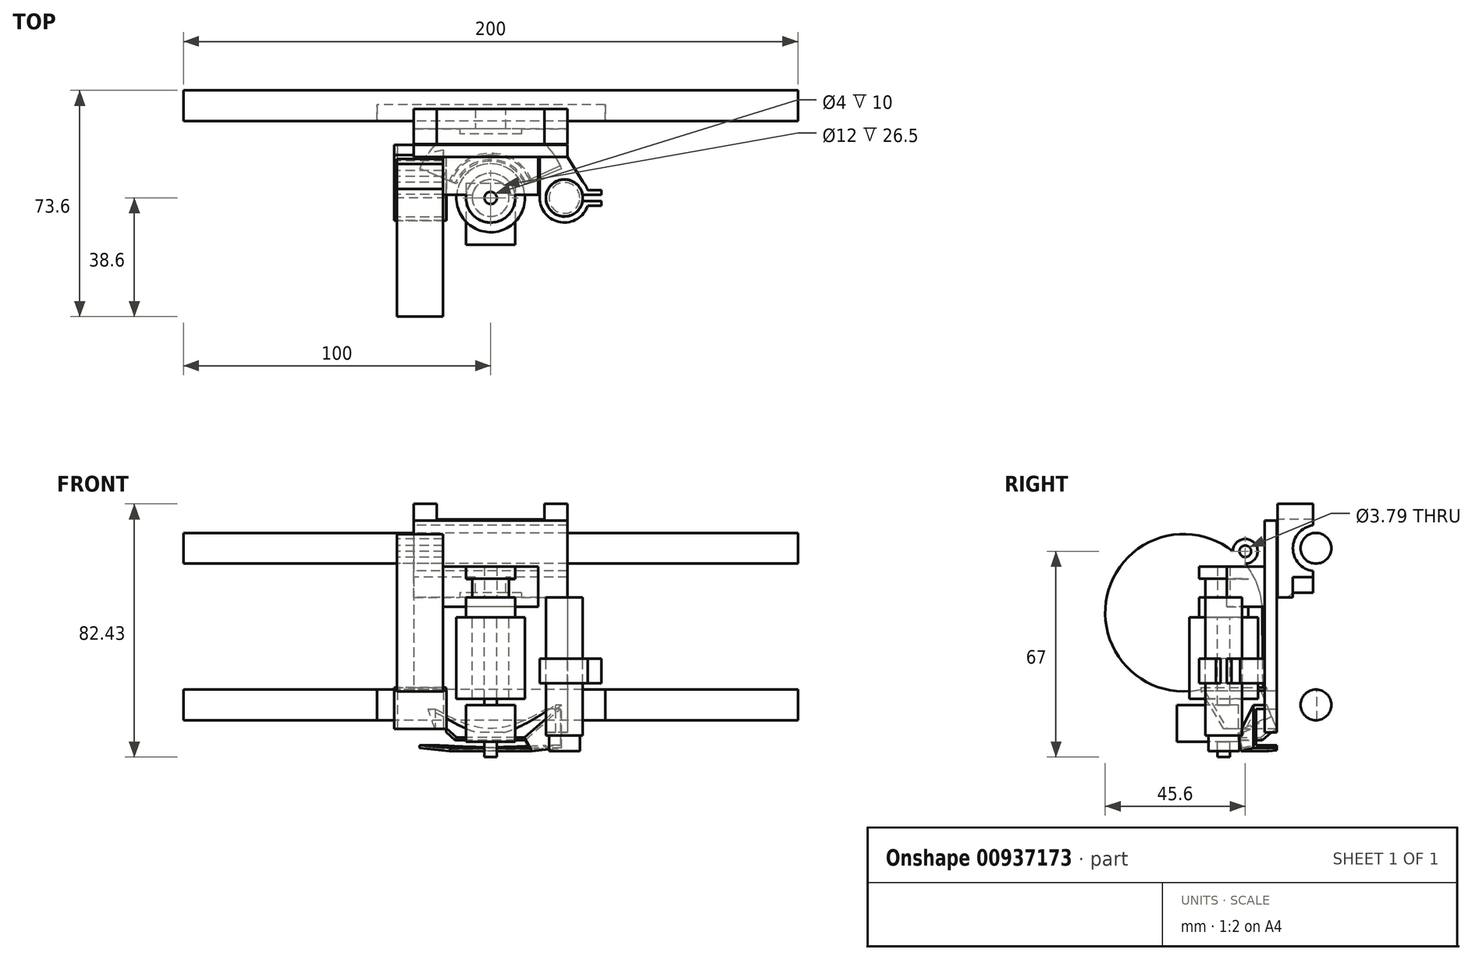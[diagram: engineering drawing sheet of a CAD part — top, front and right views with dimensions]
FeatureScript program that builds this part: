
annotation { "Feature Type Name" : "Feature", "Feature Type Description" : "" }
export const myFeature = defineFeature(function(context is Context, id is Id, definition is map)
    precondition{}
    {
        {
            var Q0;
            Q0=qCreatedBy(makeId("Top.planeOp"),FACE);
            var sketch = newSketch(context, id + "F0", { "sketchPlane" : qUnion([Q0])});
            skCircle(sketch, "E0", {"center": v(0, 0) * mm, "radius": 8 * mm});
            skCircle(sketch, "E1", {"center": v(0, 0) * mm, "radius": 6 * mm});
            skCircle(sketch, "E2", {"center": v(0, 0) * mm, "radius": 11.15 * mm});
            skCircle(sketch, "E3", {"center": v(0, 0) * mm, "radius": 2 * mm});
            skLineSegment(sketch, "E4.bottom", {"start": v(-8, 4.8) * mm, "end": v(8, 4.8) * mm});
            skLineSegment(sketch, "E4.top", {"start": v(-8, -15.2) * mm, "end": v(8, -15.2) * mm});
            skLineSegment(sketch, "E4.left", {"start": v(-8, 4.8) * mm, "end": v(-8, -15.2) * mm});
            skLineSegment(sketch, "E4.right", {"start": v(8, 4.8) * mm, "end": v(8, -15.2) * mm});
            skCircle(sketch, "E5", {"center": v(24, 0) * mm, "radius": 6 * mm});
            skCircle(sketch, "E6", {"center": v(24, 0) * mm, "radius": 5 * mm});
            skLineSegment(sketch, "E7", {"start": v(-23, 26.47) * mm, "end": v(-23, -35) * mm, "construction": true});
            skSolve(sketch);
        }
        {
            var Q0;
            Q0=makeQuery(id+"F0.imprint","IMPRINT",FACE,{"disambiguationData":[TD([[makeQuery(id+"F0.imprint","IMPRINT",EDGE,{"derivedFrom":sQuery(id+"F0.wireOp",EDGE,"E3")}),-1.0]])]});
            var Q1;
            {var subQ0=sQuery(id+"F0.wireOp",EDGE,"E4.bottom");var subQ1=sQuery(id+"F0.wireOp",EDGE,"E1");var subQ2=makeQuery(id+"F0.imprint","INTERSECT",VERTEX,{"disambiguationData":[OD(0.0)],"derivedFrom":[subQ1,subQ0]});Q1=makeQuery(id+"F0.imprint","IMPRINT",FACE,{"disambiguationData":[TD([[makeQuery(id+"F0.imprint","IMPRINT",EDGE,{"disambiguationData":[TD([[subQ2,1.0]])],"derivedFrom":subQ1}),1.0]])]});}
            extrude(context, id + "F1", {"entities" : qUnion([Q0, Q1]), "depth" : 6.05 * mm, "offsetDistance" : 25 * mm});
        }
        {
            var Q0;
            {var subQ0=sQuery(id+"F0.wireOp",EDGE,"E0");var subQ3=sQuery(id+"F0.wireOp",EDGE,"E4.bottom");var subQ8=makeQuery(id+"F0.imprint","INTERSECT",VERTEX,{"disambiguationData":[OD(0.0)],"derivedFrom":[subQ0,subQ3]});Q0=makeQuery(id+"F0.imprint","IMPRINT",FACE,{"disambiguationData":[TD([[makeQuery(id+"F0.imprint","IMPRINT",EDGE,{"disambiguationData":[TD([[subQ8,1.0]])],"derivedFrom":subQ0}),1.0]])]});}
            var Q1;
            {var subQ0=sQuery(id+"F0.wireOp",EDGE,"E4.bottom");var subQ1=sQuery(id+"F0.wireOp",EDGE,"E0");var subQ2=makeQuery(id+"F0.imprint","INTERSECT",VERTEX,{"disambiguationData":[OD(0.0)],"derivedFrom":[subQ1,subQ0]});Q1=makeQuery(id+"F0.imprint","IMPRINT",FACE,{"disambiguationData":[TD([[makeQuery(id+"F0.imprint","IMPRINT",EDGE,{"disambiguationData":[TD([[subQ2,-1.0]])],"derivedFrom":subQ1}),1.0]])]});}
            var Q2;
            Q2=makeQuery(id+"F0.imprint","IMPRINT",FACE,{"disambiguationData":[TD([[makeQuery(id+"F0.imprint","IMPRINT",EDGE,{"derivedFrom":sQuery(id+"F0.wireOp",EDGE,"E3")}),-1.0]])]});
            var Q3;
            {var subQ0=sQuery(id+"F0.wireOp",EDGE,"E4.bottom");var subQ1=sQuery(id+"F0.wireOp",EDGE,"E1");var subQ2=makeQuery(id+"F0.imprint","INTERSECT",VERTEX,{"disambiguationData":[OD(0.0)],"derivedFrom":[subQ1,subQ0]});Q3=makeQuery(id+"F0.imprint","IMPRINT",FACE,{"disambiguationData":[TD([[makeQuery(id+"F0.imprint","IMPRINT",EDGE,{"disambiguationData":[TD([[subQ2,1.0]])],"derivedFrom":subQ1}),1.0]])]});}
            extrude(context, id + "F2", {"entities" : qUnion([Q0, Q1, Q2, Q3]), "operationType" : NewBodyOperationType.ADD, "depth" : 10 * mm, "offsetDistance" : 25 * mm, "hasSecondDirection" : true, "secondDirectionOppositeDirection" : false, "secondDirectionDepth" : 6.05 * mm});
        }
        {
            var Q0;
            {var subQ0=sQuery(id+"F0.wireOp",EDGE,"E0");var subQ3=sQuery(id+"F0.wireOp",EDGE,"E4.bottom");var subQ8=makeQuery(id+"F0.imprint","INTERSECT",VERTEX,{"disambiguationData":[OD(0.0)],"derivedFrom":[subQ0,subQ3]});Q0=makeQuery(id+"F0.imprint","IMPRINT",FACE,{"disambiguationData":[TD([[makeQuery(id+"F0.imprint","IMPRINT",EDGE,{"disambiguationData":[TD([[subQ8,1.0]])],"derivedFrom":subQ0}),1.0]])]});}
            var Q1;
            {var subQ0=sQuery(id+"F0.wireOp",EDGE,"E4.bottom");var subQ1=sQuery(id+"F0.wireOp",EDGE,"E0");var subQ2=makeQuery(id+"F0.imprint","INTERSECT",VERTEX,{"disambiguationData":[OD(0.0)],"derivedFrom":[subQ1,subQ0]});Q1=makeQuery(id+"F0.imprint","IMPRINT",FACE,{"disambiguationData":[TD([[makeQuery(id+"F0.imprint","IMPRINT",EDGE,{"disambiguationData":[TD([[subQ2,-1.0]])],"derivedFrom":subQ1}),1.0]])]});}
            var Q2;
            Q2=makeQuery(id+"F0.imprint","IMPRINT",FACE,{"disambiguationData":[TD([[makeQuery(id+"F0.imprint","IMPRINT",EDGE,{"derivedFrom":sQuery(id+"F0.wireOp",EDGE,"E3")}),-1.0]])]});
            var Q3;
            {var subQ0=sQuery(id+"F0.wireOp",EDGE,"E4.bottom");var subQ1=sQuery(id+"F0.wireOp",EDGE,"E1");var subQ2=makeQuery(id+"F0.imprint","INTERSECT",VERTEX,{"disambiguationData":[OD(0.0)],"derivedFrom":[subQ1,subQ0]});Q3=makeQuery(id+"F0.imprint","IMPRINT",FACE,{"disambiguationData":[TD([[makeQuery(id+"F0.imprint","IMPRINT",EDGE,{"disambiguationData":[TD([[subQ2,1.0]])],"derivedFrom":subQ1}),1.0]])]});}
            extrude(context, id + "F3", {"entities" : qUnion([Q0, Q1, Q2, Q3]), "operationType" : NewBodyOperationType.ADD, "oppositeDirection" : true, "depth" : 6.5 * mm, "offsetDistance" : 25 * mm});
        }
        {
            var Q0;
            {var subQ0=sQuery(id+"F0.wireOp",EDGE,"E4.right");var subQ1=sQuery(id+"F0.wireOp",EDGE,"E0");var subQ2=makeQuery(id+"F0.imprint","INTERSECT",VERTEX,{"derivedFrom":[subQ1,subQ0]});Q0=makeQuery(id+"F0.imprint","IMPRINT",FACE,{"disambiguationData":[TD([[makeQuery(id+"F0.imprint","IMPRINT",EDGE,{"disambiguationData":[TD([[subQ2,1.0]])],"derivedFrom":subQ1}),-1.0]])]});}
            var Q1;
            {var subQ1=sQuery(id+"F0.wireOp",EDGE,"E4.bottom");var subQ3=sQuery(id+"F0.wireOp",EDGE,"E0");var subQ4=makeQuery(id+"F0.imprint","INTERSECT",VERTEX,{"disambiguationData":[OD(0.0)],"derivedFrom":[subQ3,subQ1]});Q1=makeQuery(id+"F0.imprint","IMPRINT",FACE,{"disambiguationData":[TD([[makeQuery(id+"F0.imprint","IMPRINT",EDGE,{"disambiguationData":[TD([[subQ4,-1.0]])],"derivedFrom":subQ3}),-1.0]])]});}
            var Q2;
            {var subQ0=sQuery(id+"F0.wireOp",EDGE,"E4.bottom");var subQ1=sQuery(id+"F0.wireOp",EDGE,"E0");var subQ2=makeQuery(id+"F0.imprint","INTERSECT",VERTEX,{"disambiguationData":[OD(0.0)],"derivedFrom":[subQ1,subQ0]});Q2=makeQuery(id+"F0.imprint","IMPRINT",FACE,{"disambiguationData":[TD([[makeQuery(id+"F0.imprint","IMPRINT",EDGE,{"disambiguationData":[TD([[subQ2,-1.0]])],"derivedFrom":subQ1}),1.0]])]});}
            var Q3;
            {var subQ0=sQuery(id+"F0.wireOp",EDGE,"E0");var subQ3=sQuery(id+"F0.wireOp",EDGE,"E4.bottom");var subQ8=makeQuery(id+"F0.imprint","INTERSECT",VERTEX,{"disambiguationData":[OD(0.0)],"derivedFrom":[subQ0,subQ3]});Q3=makeQuery(id+"F0.imprint","IMPRINT",FACE,{"disambiguationData":[TD([[makeQuery(id+"F0.imprint","IMPRINT",EDGE,{"disambiguationData":[TD([[subQ8,1.0]])],"derivedFrom":subQ0}),1.0]])]});}
            var Q4;
            {var subQ0=sQuery(id+"F0.wireOp",EDGE,"E4.bottom");var subQ1=sQuery(id+"F0.wireOp",EDGE,"E0");var subQ2=makeQuery(id+"F0.imprint","INTERSECT",VERTEX,{"disambiguationData":[OD(0.0)],"derivedFrom":[subQ1,subQ0]});Q4=makeQuery(id+"F0.imprint","IMPRINT",FACE,{"disambiguationData":[TD([[makeQuery(id+"F0.imprint","IMPRINT",EDGE,{"disambiguationData":[TD([[subQ2,1.0]])],"derivedFrom":subQ1}),-1.0]])]});}
            var Q5;
            {var subQ0=sQuery(id+"F0.wireOp",EDGE,"E4.bottom");var subQ1=sQuery(id+"F0.wireOp",EDGE,"E0");var subQ2=makeQuery(id+"F0.imprint","INTERSECT",VERTEX,{"disambiguationData":[OD(1.0)],"derivedFrom":[subQ1,subQ0]});Q5=makeQuery(id+"F0.imprint","IMPRINT",FACE,{"disambiguationData":[TD([[makeQuery(id+"F0.imprint","IMPRINT",EDGE,{"disambiguationData":[TD([[subQ2,-1.0]])],"derivedFrom":subQ1}),-1.0]])]});}
            extrude(context, id + "F4", {"entities" : qUnion([Q0, Q1, Q2, Q3, Q4, Q5]), "operationType" : NewBodyOperationType.ADD, "oppositeDirection" : true, "depth" : 33 * mm, "offsetDistance" : 25 * mm, "hasSecondDirection" : true, "secondDirectionOppositeDirection" : true, "secondDirectionDepth" : 6.5 * mm});
        }
        {
            var Q0;
            Q0=makeQuery(id+"F0.imprint","IMPRINT",FACE,{"disambiguationData":[TD([[makeQuery(id+"F0.imprint","IMPRINT",EDGE,{"derivedFrom":sQuery(id+"F0.wireOp",EDGE,"E3")}),1.0]])]});
            extrude(context, id + "F5", {"entities" : qUnion([Q0]), "operationType" : NewBodyOperationType.ADD, "oppositeDirection" : true, "depth" : 52 * mm, "offsetDistance" : 25 * mm});
        }
        {
            var Q0;
            {var subQ5=sQuery(id+"F0.wireOp",EDGE,"E4.top");Q0=makeQuery(id+"F0.imprint","IMPRINT",FACE,{"disambiguationData":[TD([[makeQuery(id+"F0.imprint","IMPRINT",EDGE,{"derivedFrom":subQ5}),1.0]])]});}
            var Q1;
            {var subQ0=sQuery(id+"F0.wireOp",EDGE,"E4.right");var subQ1=sQuery(id+"F0.wireOp",EDGE,"E0");var subQ2=makeQuery(id+"F0.imprint","INTERSECT",VERTEX,{"derivedFrom":[subQ1,subQ0]});Q1=makeQuery(id+"F0.imprint","IMPRINT",FACE,{"disambiguationData":[TD([[makeQuery(id+"F0.imprint","IMPRINT",EDGE,{"disambiguationData":[TD([[subQ2,1.0]])],"derivedFrom":subQ1}),-1.0]])]});}
            var Q2;
            {var subQ0=sQuery(id+"F0.wireOp",EDGE,"E4.bottom");var subQ1=sQuery(id+"F0.wireOp",EDGE,"E0");var subQ2=makeQuery(id+"F0.imprint","INTERSECT",VERTEX,{"disambiguationData":[OD(0.0)],"derivedFrom":[subQ1,subQ0]});Q2=makeQuery(id+"F0.imprint","IMPRINT",FACE,{"disambiguationData":[TD([[makeQuery(id+"F0.imprint","IMPRINT",EDGE,{"disambiguationData":[TD([[subQ2,1.0]])],"derivedFrom":subQ1}),-1.0]])]});}
            var Q3;
            {var subQ0=sQuery(id+"F0.wireOp",EDGE,"E0");var subQ3=sQuery(id+"F0.wireOp",EDGE,"E4.bottom");var subQ8=makeQuery(id+"F0.imprint","INTERSECT",VERTEX,{"disambiguationData":[OD(0.0)],"derivedFrom":[subQ0,subQ3]});Q3=makeQuery(id+"F0.imprint","IMPRINT",FACE,{"disambiguationData":[TD([[makeQuery(id+"F0.imprint","IMPRINT",EDGE,{"disambiguationData":[TD([[subQ8,1.0]])],"derivedFrom":subQ0}),1.0]])]});}
            var Q4;
            {var subQ0=sQuery(id+"F0.wireOp",EDGE,"E4.bottom");var subQ1=sQuery(id+"F0.wireOp",EDGE,"E0");var subQ2=makeQuery(id+"F0.imprint","INTERSECT",VERTEX,{"disambiguationData":[OD(1.0)],"derivedFrom":[subQ1,subQ0]});Q4=makeQuery(id+"F0.imprint","IMPRINT",FACE,{"disambiguationData":[TD([[makeQuery(id+"F0.imprint","IMPRINT",EDGE,{"disambiguationData":[TD([[subQ2,-1.0]])],"derivedFrom":subQ1}),-1.0]])]});}
            var Q5;
            Q5=makeQuery(id+"F0.imprint","IMPRINT",FACE,{"disambiguationData":[TD([[makeQuery(id+"F0.imprint","IMPRINT",EDGE,{"derivedFrom":sQuery(id+"F0.wireOp",EDGE,"E3")}),-1.0]])]});
            var Q6;
            Q6=makeQuery(id+"F0.imprint","IMPRINT",FACE,{"disambiguationData":[TD([[makeQuery(id+"F0.imprint","IMPRINT",EDGE,{"derivedFrom":sQuery(id+"F0.wireOp",EDGE,"E3")}),1.0]])]});
            extrude(context, id + "F6", {"entities" : qUnion([Q0, Q1, Q2, Q3, Q4, Q5, Q6]), "operationType" : NewBodyOperationType.ADD, "oppositeDirection" : true, "depth" : 47 * mm, "offsetDistance" : 25 * mm, "hasSecondDirection" : true, "secondDirectionOppositeDirection" : true, "secondDirectionDepth" : 35 * mm});
        }
        {
            var Q0;
            Q0=qCreatedBy(makeId("Right.planeOp"),FACE);
            var sketch = newSketch(context, id + "F7", { "sketchPlane" : qUnion([Q0])});
            skCircle(sketch, "E8", {"center": v(30, -35) * mm, "radius": 5 * mm});
            skCircle(sketch, "E9", {"center": v(30, 16) * mm, "radius": 5 * mm});
            skLineSegment(sketch, "E10", {"start": v(30, 47) * mm, "end": v(30, -80.34) * mm, "construction": true});
            skSolve(sketch);
        }
        {
            var Q0;
            Q0=makeQuery(id+"F7.imprint","IMPRINT",FACE,{"disambiguationData":[TD([[makeQuery(id+"F7.imprint","IMPRINT",EDGE,{"derivedFrom":sQuery(id+"F7.wireOp",EDGE,"E9")}),1.0]])]});
            var Q1;
            Q1=makeQuery(id+"F7.imprint","IMPRINT",FACE,{"disambiguationData":[TD([[makeQuery(id+"F7.imprint","IMPRINT",EDGE,{"derivedFrom":sQuery(id+"F7.wireOp",EDGE,"E8")}),1.0]])]});
            extrude(context, id + "F8", {"entities" : qUnion([Q0, Q1]), "endBound" : BoundingType.SYMMETRIC, "depth" : 200 * mm, "offsetDistance" : 25 * mm});
        }
        {
            var Q0;
            Q0=qCreatedBy(makeId("Right.planeOp"),FACE);
            var sketch = newSketch(context, id + "F9", { "sketchPlane" : qUnion([Q0])});
            skCircle(sketch, "E11", {"center": v(30, 16) * mm, "radius": 6.05 * mm});
            skCircle(sketch, "E12", {"center": v(30, 16) * mm, "radius": 7.45 * mm});
            skCircle(sketch, "E13", {"center": v(30, -35) * mm, "radius": 6.05 * mm});
            skCircle(sketch, "E14", {"center": v(30, -35) * mm, "radius": 7.45 * mm});
            skArc(sketch, "E15", {"start": v(29, 23.43) * mm, "mid": v(22.5, 16) * mm, "end": v(29, 8.57) * mm});
            skArc(sketch, "E16", {"start": v(29, -27.57) * mm, "mid": v(22.5, -35) * mm, "end": v(29, -42.43) * mm});
            skLineSegment(sketch, "E17", {"start": v(29, 23.43) * mm, "end": v(29, 30.43) * mm});
            skLineSegment(sketch, "E18", {"start": v(29, -42.43) * mm, "end": v(29, -49.5) * mm});
            skLineSegment(sketch, "E19", {"start": v(29, -49.5) * mm, "end": v(17.5, -49.5) * mm});
            skLineSegment(sketch, "E20", {"start": v(17.5, -49.5) * mm, "end": v(17.5, 30.43) * mm});
            skLineSegment(sketch, "E21", {"start": v(17.5, 30.43) * mm, "end": v(29, 30.43) * mm});
            skLineSegment(sketch, "E22", {"start": v(29, -27.57) * mm, "end": v(29, -20.57) * mm});
            skLineSegment(sketch, "E23", {"start": v(29, -20.57) * mm, "end": v(22.5, -20.57) * mm});
            skLineSegment(sketch, "E24", {"start": v(22.5, -20.57) * mm, "end": v(22.5, 1.57) * mm});
            skLineSegment(sketch, "E25", {"start": v(22.5, 1.57) * mm, "end": v(29, 1.57) * mm});
            skLineSegment(sketch, "E26", {"start": v(29, 1.57) * mm, "end": v(29, 8.57) * mm});
            skLineSegment(sketch, "E27", {"start": v(29, 25.43) * mm, "end": v(17.5, 25.43) * mm});
            skLineSegment(sketch, "E28", {"start": v(29, 6.57) * mm, "end": v(17.5, 6.57) * mm});
            skLineSegment(sketch, "E29", {"start": v(29, -25.57) * mm, "end": v(17.5, -25.57) * mm});
            skLineSegment(sketch, "E30", {"start": v(29, -44.43) * mm, "end": v(17.5, -44.43) * mm});
            skLineSegment(sketch, "E31", {"start": v(17.5, -28.91) * mm, "end": v(25.75, -20.57) * mm});
            skLineSegment(sketch, "E32", {"start": v(17.5, -3.22) * mm, "end": v(22.5, 1.57) * mm});
            skLineSegment(sketch, "E33", {"start": v(22.5, 1.57) * mm, "end": v(22.5, 6.57) * mm});
            skLineSegment(sketch, "E34", {"start": v(22.5, -20.57) * mm, "end": v(22.5, -25.57) * mm});
            skSolve(sketch);
        }
        {
            var Q0;
            {var subQ1=sQuery(id+"F9.wireOp",EDGE,"E16");Q0=makeQuery(id+"F9.imprint","IMPRINT",FACE,{"disambiguationData":[TD([[makeQuery(id+"F9.imprint","IMPRINT",EDGE,{"derivedFrom":subQ1}),-1.0]])]});}
            var Q1;
            {var subQ0=sQuery(id+"F9.wireOp",EDGE,"E29");var subQ1=sQuery(id+"F9.wireOp",EDGE,"E20");var subQ2=makeQuery(id+"F9.imprint","INTERSECT",VERTEX,{"derivedFrom":[subQ1,subQ0]});Q1=makeQuery(id+"F9.imprint","IMPRINT",FACE,{"disambiguationData":[TD([[makeQuery(id+"F9.imprint","IMPRINT",EDGE,{"disambiguationData":[TD([[subQ2,1.0]])],"derivedFrom":subQ1}),-1.0]])]});}
            var Q2;
            {var subQ0=sQuery(id+"F9.wireOp",EDGE,"E34");var subQ1=sQuery(id+"F9.wireOp",EDGE,"E29");var subQ2=makeQuery(id+"F9.imprint","INTERSECT",VERTEX,{"derivedFrom":[subQ1,subQ0]});Q2=makeQuery(id+"F9.imprint","IMPRINT",FACE,{"disambiguationData":[TD([[makeQuery(id+"F9.imprint","IMPRINT",EDGE,{"disambiguationData":[TD([[subQ2,-1.0]])],"derivedFrom":subQ1}),-1.0]])]});}
            var Q3;
            {var subQ7=sQuery(id+"F9.wireOp",EDGE,"E24");Q3=makeQuery(id+"F9.imprint","IMPRINT",FACE,{"disambiguationData":[TD([[makeQuery(id+"F9.imprint","IMPRINT",EDGE,{"derivedFrom":subQ7}),1.0]])]});}
            var Q4;
            {var subQ3=sQuery(id+"F9.wireOp",EDGE,"E32");Q4=makeQuery(id+"F9.imprint","IMPRINT",FACE,{"disambiguationData":[TD([[makeQuery(id+"F9.imprint","IMPRINT",EDGE,{"derivedFrom":subQ3}),1.0]])]});}
            var Q5;
            {var subQ1=sQuery(id+"F9.wireOp",EDGE,"E15");Q5=makeQuery(id+"F9.imprint","IMPRINT",FACE,{"disambiguationData":[TD([[makeQuery(id+"F9.imprint","IMPRINT",EDGE,{"derivedFrom":subQ1}),-1.0]])]});}
            var Q6;
            {var subQ0=sQuery(id+"F9.wireOp",EDGE,"E21");Q6=makeQuery(id+"F9.imprint","IMPRINT",FACE,{"disambiguationData":[TD([[makeQuery(id+"F9.imprint","IMPRINT",EDGE,{"derivedFrom":subQ0}),-1.0]])]});}
            var Q7;
            {var subQ0=sQuery(id+"F9.wireOp",EDGE,"E19");Q7=makeQuery(id+"F9.imprint","IMPRINT",FACE,{"disambiguationData":[TD([[makeQuery(id+"F9.imprint","IMPRINT",EDGE,{"derivedFrom":subQ0}),-1.0]])]});}
            extrude(context, id + "F10", {"entities" : qUnion([Q0, Q1, Q2, Q3, Q4, Q5, Q6, Q7]), "endBound" : BoundingType.SYMMETRIC, "depth" : 50 * mm, "offsetDistance" : 25 * mm});
        }
        {
            var Q0;
            {var subQ0=sQuery(id+"F9.wireOp",EDGE,"E21");Q0=makeQuery(id+"F9.imprint","IMPRINT",FACE,{"disambiguationData":[TD([[makeQuery(id+"F9.imprint","IMPRINT",EDGE,{"derivedFrom":subQ0}),-1.0]])]});}
            extrude(context, id + "F11", {"entities" : qUnion([Q0]), "operationType" : NewBodyOperationType.REMOVE, "endBound" : BoundingType.SYMMETRIC, "oppositeDirection" : true, "depth" : 35 * mm, "offsetDistance" : 25 * mm});
        }
        {
            var Q0;
            {var subQ0=sQuery(id+"F9.wireOp",EDGE,"E25");Q0=makeQuery(id+"F9.imprint","IMPRINT",FACE,{"disambiguationData":[TD([[makeQuery(id+"F9.imprint","IMPRINT",EDGE,{"derivedFrom":subQ0}),1.0]])]});}
            var Q1;
            {var subQ1=sQuery(id+"F9.wireOp",EDGE,"E23");var subQ5=sQuery(id+"F9.wireOp",EDGE,"E22");var subQ6=makeQuery(id+"F9.imprint","INTERSECT",VERTEX,{"derivedFrom":[subQ5,subQ1]});Q1=makeQuery(id+"F9.imprint","IMPRINT",FACE,{"disambiguationData":[TD([[makeQuery(id+"F9.imprint","IMPRINT",EDGE,{"disambiguationData":[TD([[subQ6,1.0]])],"derivedFrom":subQ5}),1.0]])]});}
            extrude(context, id + "F12", {"entities" : qUnion([Q0, Q1]), "operationType" : NewBodyOperationType.ADD, "endBound" : BoundingType.SYMMETRIC, "depth" : 10 * mm, "offsetDistance" : 25 * mm});
        }
        {
            var Q0;
            {var subQ7=sQuery(id+"F9.wireOp",EDGE,"E24");Q0=makeQuery(id+"F9.imprint","IMPRINT",FACE,{"disambiguationData":[TD([[makeQuery(id+"F9.imprint","IMPRINT",EDGE,{"derivedFrom":subQ7}),1.0]])]});}
            var Q1;
            {var subQ0=sQuery(id+"F9.wireOp",EDGE,"E29");var subQ1=sQuery(id+"F9.wireOp",EDGE,"E20");var subQ2=makeQuery(id+"F9.imprint","INTERSECT",VERTEX,{"derivedFrom":[subQ1,subQ0]});Q1=makeQuery(id+"F9.imprint","IMPRINT",FACE,{"disambiguationData":[TD([[makeQuery(id+"F9.imprint","IMPRINT",EDGE,{"disambiguationData":[TD([[subQ2,1.0]])],"derivedFrom":subQ1}),-1.0]])]});}
            extrude(context, id + "F13", {"entities" : qUnion([Q0, Q1]), "operationType" : NewBodyOperationType.REMOVE, "endBound" : BoundingType.SYMMETRIC, "depth" : 20 * mm, "offsetDistance" : 25 * mm});
        }
        {
            var Q0;
            Q0=makeQuery(id+"F0.imprint","IMPRINT",FACE,{"disambiguationData":[TD([[makeQuery(id+"F0.imprint","IMPRINT",EDGE,{"derivedFrom":sQuery(id+"F0.wireOp",EDGE,"E6")}),1.0]])]});
            extrude(context, id + "F14", {"entities" : qUnion([Q0]), "oppositeDirection" : true, "depth" : 50 * mm, "offsetDistance" : 25 * mm});
        }
        {
            var Q0;
            Q0=makeQuery(id+"F0.imprint","IMPRINT",FACE,{"disambiguationData":[TD([[makeQuery(id+"F0.imprint","IMPRINT",EDGE,{"derivedFrom":sQuery(id+"F0.wireOp",EDGE,"E5")}),1.0]])]});
            extrude(context, id + "F15", {"entities" : qUnion([Q0]), "operationType" : NewBodyOperationType.ADD, "oppositeDirection" : true, "depth" : 45 * mm, "offsetDistance" : 25 * mm});
        }
        {
            var Q0;
            Q0=sQuery(id+"F0.wireOp",EDGE,"E7");
            cPlane(context, id + "F16", {"entities" : qUnion([Q0]), "cplaneType" : CPlaneType.LINE_ANGLE, "offset" : 25 * mm, "angle" : 90 * degree, "width" : 150 * mm, "height" : 150 * mm});
        }
        {
            var Q0;
            Q0=qCreatedBy(id+"F16.planeOp",FACE);
            var sketch = newSketch(context, id + "F17", { "sketchPlane" : qUnion([Q0])});
            skCircle(sketch, "E35", {"center": v(-13, -5) * mm, "radius": 25.6 * mm});
            skLineSegment(sketch, "E36", {"start": v(12.77, -30.4) * mm, "end": v(-6.23, -30.4) * mm});
            skLineSegment(sketch, "E37", {"start": v(-6.23, -30.4) * mm, "end": v(-6.23, -29.69) * mm});
            skCircle(sketch, "E38", {"center": v(7, 15) * mm, "radius": 1.9 * mm});
            skLineSegment(sketch, "E39", {"start": v(12.77, -30.4) * mm, "end": v(12.6, -4.83) * mm});
            skArc(sketch, "E40", {"start": v(7, 10.98) * mm, "mid": v(9.84, 17.84) * mm, "end": v(2.98, 15) * mm});
            skSolve(sketch);
        }
        {
            var Q0;
            {var subQ0=sQuery(id+"F17.wireOp",EDGE,"E35");var subQ1=makeQuery(id+"F17.imprint","INTERSECT",VERTEX,{"derivedFrom":[subQ0,sQuery(id+"F17.wireOp",EDGE,"E39")]});Q0=makeQuery(id+"F17.imprint","IMPRINT",FACE,{"disambiguationData":[TD([[makeQuery(id+"F17.imprint","IMPRINT",EDGE,{"disambiguationData":[TD([[subQ1,-1.0]])],"derivedFrom":subQ0}),1.0]])]});}
            var Q1;
            Q1=makeQuery(id+"F17.imprint","IMPRINT",FACE,{"disambiguationData":[TD([[makeQuery(id+"F17.imprint","IMPRINT",EDGE,{"derivedFrom":sQuery(id+"F17.wireOp",EDGE,"E36")}),-1.0]])]});
            var Q2;
            Q2=makeQuery(id+"F17.imprint","IMPRINT",FACE,{"disambiguationData":[TD([[makeQuery(id+"F17.imprint","IMPRINT",EDGE,{"derivedFrom":sQuery(id+"F17.wireOp",EDGE,"E38")}),-1.0]])]});
            extrude(context, id + "F18", {"entities" : qUnion([Q0, Q1, Q2]), "endBound" : BoundingType.SYMMETRIC, "depth" : 15 * mm, "offsetDistance" : 25 * mm});
        }
        {
            var Q0;
            Q0=qCreatedBy(makeId("Top.planeOp"),FACE);
            var sketch = newSketch(context, id + "F19", { "sketchPlane" : qUnion([Q0])});
            skLineSegment(sketch, "E41", {"start": v(-25, 17.3) * mm, "end": v(25, 17.3) * mm});
            skLineSegment(sketch, "E42", {"start": v(25, 17.3) * mm, "end": v(25, 13.3) * mm});
            skLineSegment(sketch, "E43", {"start": v(25, 13.3) * mm, "end": v(-25, 13.3) * mm});
            skLineSegment(sketch, "E44", {"start": v(-25, 13.3) * mm, "end": v(-25, 17.3) * mm});
            skLineSegment(sketch, "E45", {"start": v(-15.5, 13.3) * mm, "end": v(-15.5, 1) * mm});
            skLineSegment(sketch, "E46", {"start": v(-15.5, 1) * mm, "end": v(-5.92, 1) * mm});
            skLineSegment(sketch, "E47", {"start": v(5.92, 1) * mm, "end": v(15.5, 1) * mm});
            skLineSegment(sketch, "E48", {"start": v(15.5, 1) * mm, "end": v(15.5, 13.3) * mm});
            skCircle(sketch, "E49", {"center": v(0, 0) * mm, "radius": 6 * mm});
            skCircle(sketch, "E50", {"center": v(0, 0) * mm, "radius": 8 * mm});
            skLineSegment(sketch, "E51", {"start": v(25, 13.3) * mm, "end": v(29.97, 5.32) * mm});
            skCircle(sketch, "E52", {"center": v(24, 0) * mm, "radius": 6.05 * mm});
            skLineSegment(sketch, "E53", {"start": v(16, 13.3) * mm, "end": v(16, 0) * mm});
            skArc(sketch, "E54", {"start": v(16, 0) * mm, "mid": v(22.73, -7.9) * mm, "end": v(31.6, -2.5) * mm});
            skArc(sketch, "E55", {"start": v(31.6, 2.5) * mm, "mid": v(30.93, 4) * mm, "end": v(29.97, 5.32) * mm});
            skLineSegment(sketch, "E56", {"start": v(29.97, 1) * mm, "end": v(36, 1) * mm});
            skLineSegment(sketch, "E57", {"start": v(36, 1) * mm, "end": v(36, 2.5) * mm});
            skLineSegment(sketch, "E58", {"start": v(36, 2.5) * mm, "end": v(31.6, 2.5) * mm});
            skLineSegment(sketch, "E59", {"start": v(31.6, -2.5) * mm, "end": v(36, -2.5) * mm});
            skLineSegment(sketch, "E60", {"start": v(36, -2.5) * mm, "end": v(36, -1) * mm});
            skLineSegment(sketch, "E61", {"start": v(36, -1) * mm, "end": v(29.97, -1) * mm});
            skLineSegment(sketch, "E62.bottom", {"start": v(-36.99, 17.3) * mm, "end": v(37.28, 17.3) * mm});
            skLineSegment(sketch, "E62.top", {"start": v(-36.99, 30.37) * mm, "end": v(37.28, 30.37) * mm});
            skLineSegment(sketch, "E62.left", {"start": v(-36.99, 17.3) * mm, "end": v(-36.99, 30.37) * mm});
            skLineSegment(sketch, "E62.right", {"start": v(37.28, 17.3) * mm, "end": v(37.28, 30.37) * mm});
            skSolve(sketch);
        }
        {
            var Q0;
            {var subQ4=sQuery(id+"F19.wireOp",EDGE,"E42");Q0=makeQuery(id+"F19.imprint","IMPRINT",FACE,{"disambiguationData":[TD([[makeQuery(id+"F19.imprint","IMPRINT",EDGE,{"derivedFrom":subQ4}),-1.0]])]});}
            extrude(context, id + "F20", {"entities" : qUnion([Q0]), "depth" : 25 * mm, "offsetDistance" : 25 * mm});
        }
        {
            var Q0;
            {var subQ4=sQuery(id+"F19.wireOp",EDGE,"E42");Q0=makeQuery(id+"F19.imprint","IMPRINT",FACE,{"disambiguationData":[TD([[makeQuery(id+"F19.imprint","IMPRINT",EDGE,{"derivedFrom":subQ4}),-1.0]])]});}
            extrude(context, id + "F21", {"entities" : qUnion([Q0]), "operationType" : NewBodyOperationType.ADD, "oppositeDirection" : true, "depth" : 44 * mm, "offsetDistance" : 25 * mm});
        }
        {
            var Q0;
            {var subQ5=sQuery(id+"F19.wireOp",EDGE,"E45");Q0=makeQuery(id+"F19.imprint","IMPRINT",FACE,{"disambiguationData":[TD([[makeQuery(id+"F19.imprint","IMPRINT",EDGE,{"derivedFrom":subQ5}),1.0]])]});}
            extrude(context, id + "F22", {"entities" : qUnion([Q0]), "operationType" : NewBodyOperationType.ADD, "oppositeDirection" : true, "depth" : 3 * mm, "offsetDistance" : 25 * mm});
        }
        {
            var Q0;
            {var subQ0=sQuery(id+"F19.wireOp",EDGE,"E49");var subQ1=sQuery(id+"F19.wireOp",EDGE,"E46");var subQ2=makeQuery(id+"F19.imprint","INTERSECT",VERTEX,{"derivedFrom":[subQ1,subQ0]});Q0=makeQuery(id+"F19.imprint","IMPRINT",FACE,{"disambiguationData":[TD([[makeQuery(id+"F19.imprint","IMPRINT",EDGE,{"disambiguationData":[TD([[subQ2,1.0]])],"derivedFrom":subQ1}),1.0]])]});}
            var Q1;
            {var subQ5=sQuery(id+"F19.wireOp",EDGE,"E45");Q1=makeQuery(id+"F19.imprint","IMPRINT",FACE,{"disambiguationData":[TD([[makeQuery(id+"F19.imprint","IMPRINT",EDGE,{"derivedFrom":subQ5}),1.0]])]});}
            extrude(context, id + "F23", {"entities" : qUnion([Q0, Q1]), "operationType" : NewBodyOperationType.ADD, "depth" : 6 * mm, "offsetDistance" : 25 * mm});
        }
        {
            var Q0;
            {var subQ5=sQuery(id+"F19.wireOp",EDGE,"E45");Q0=makeQuery(id+"F19.imprint","IMPRINT",FACE,{"disambiguationData":[TD([[makeQuery(id+"F19.imprint","IMPRINT",EDGE,{"derivedFrom":subQ5}),1.0]])]});}
            extrude(context, id + "F24", {"entities" : qUnion([Q0]), "operationType" : NewBodyOperationType.ADD, "depth" : 10 * mm, "offsetDistance" : 25 * mm});
        }
        {
            var Q0;
            {var subQ0=sQuery(id+"F19.wireOp",EDGE,"E51");Q0=makeQuery(id+"F19.imprint","IMPRINT",FACE,{"disambiguationData":[TD([[makeQuery(id+"F19.imprint","IMPRINT",EDGE,{"derivedFrom":subQ0}),-1.0]])]});}
            extrude(context, id + "F25", {"entities" : qUnion([Q0]), "operationType" : NewBodyOperationType.ADD, "oppositeDirection" : true, "depth" : 28 * mm, "offsetDistance" : 25 * mm, "hasSecondDirection" : true, "secondDirectionOppositeDirection" : true, "secondDirectionDepth" : 20 * mm});
        }
        {
            var Q0;
            Q0=qCreatedBy(makeId("Right.planeOp"),FACE);
            var sketch = newSketch(context, id + "F26", { "sketchPlane" : qUnion([Q0])});
            skLineSegment(sketch, "E63", {"start": v(14, -49.04) * mm, "end": v(25, -48.08) * mm});
            skLineSegment(sketch, "E64", {"start": v(12.5, -46.45) * mm, "end": v(25, -36.29) * mm});
            skLineSegment(sketch, "E65", {"start": v(25, -36.29) * mm, "end": v(25, -35) * mm});
            skLineSegment(sketch, "E66", {"start": v(25, -35) * mm, "end": v(12, -45.57) * mm});
            skLineSegment(sketch, "E67", {"start": v(12, -45.57) * mm, "end": v(14.56, -50) * mm});
            skLineSegment(sketch, "E68", {"start": v(14.56, -50) * mm, "end": v(25, -49.09) * mm});
            skLineSegment(sketch, "E69", {"start": v(25, -49.09) * mm, "end": v(25, -48.08) * mm});
            skLineSegment(sketch, "E70", {"start": v(25, -36.29) * mm, "end": v(25, -48.08) * mm});
            skLineSegment(sketch, "E71", {"start": v(0, 56.21) * mm, "end": v(0, -85.2) * mm, "construction": true});
            skSolve(sketch);
        }
        {
            var Q0;
            {var subQ0=sQuery(id+"F26.wireOp",EDGE,"E64");Q0=makeQuery(id+"F26.imprint","IMPRINT",FACE,{"disambiguationData":[TD([[makeQuery(id+"F26.imprint","IMPRINT",EDGE,{"derivedFrom":subQ0}),1.0]])]});}
            var Q1;
            {var subQ0=sQuery(id+"F26.wireOp",EDGE,"E63");Q1=makeQuery(id+"F26.imprint","IMPRINT",FACE,{"disambiguationData":[TD([[makeQuery(id+"F26.imprint","IMPRINT",EDGE,{"derivedFrom":subQ0}),1.0]])]});}
            var Q2;
            {var subQ0=sQuery(id+"F26.wireOp",EDGE,"E63");Q2=makeQuery(id+"F26.imprint","IMPRINT",FACE,{"disambiguationData":[TD([[makeQuery(id+"F26.imprint","IMPRINT",EDGE,{"derivedFrom":subQ0}),-1.0]])]});}
            var Q3;
            Q3=sQuery(id+"F26.wireOp",EDGE,"E71");
            revolve(context, id + "F27", {"operationType" : NewBodyOperationType.ADD, "surfaceOperationType" : NewSurfaceOperationType.NEW, "entities" : qUnion([Q0, Q1, Q2]), "axis" : qUnion([Q3]), "revolveType" : RevolveType.SYMMETRIC, "angle" : 135 * degree});
        }
        {
            var Q0;
            {var subQ0=sQuery(id+"F26.wireOp",EDGE,"E63");Q0=makeQuery(id+"F26.imprint","IMPRINT",FACE,{"disambiguationData":[TD([[makeQuery(id+"F26.imprint","IMPRINT",EDGE,{"derivedFrom":subQ0}),1.0]])]});}
            var Q1;
            Q1=sQuery(id+"F26.wireOp",EDGE,"E71");
            revolve(context, id + "F28", {"operationType" : NewBodyOperationType.REMOVE, "surfaceOperationType" : NewSurfaceOperationType.NEW, "entities" : qUnion([Q0]), "axis" : qUnion([Q1]), "revolveType" : RevolveType.SYMMETRIC, "angle" : 130 * degree});
        }
        {
            var Q0;
            Q0=makeQuery(id+"F28.boolean.opBoolean","COPY",FACE,{"derivedFrom":makeQuery(id+"F28.opRevolve","CAP_FACE",FACE,{"disambiguationData":[OSD([sQuery(id+"F26.wireOp",EDGE,"E63"),sQuery(id+"F26.wireOp",EDGE,"E64"),sQuery(id+"F26.wireOp",EDGE,"E67"),sQuery(id+"F26.wireOp",EDGE,"E70")])],"isStart":true})});
            extrude(context, id + "F29", {"entities" : qUnion([Q0]), "operationType" : NewBodyOperationType.REMOVE, "oppositeDirection" : true, "depth" : 25 * mm, "offsetDistance" : 25 * mm});
        }
        {
            var Q0;
            Q0=makeQuery(id+"F18.opExtrude","SWEPT_FACE",FACE,{"disambiguationData":[OSD([sQuery(id+"F17.wireOp",EDGE,"E36")])]});
            var sketch = newSketch(context, id + "F30", { "sketchPlane" : qUnion([Q0])});
            skLineSegment(sketch, "E72.bottom", {"start": v(-30.5, 6.23) * mm, "end": v(-15.5, 6.23) * mm});
            skLineSegment(sketch, "E72.top", {"start": v(-30.5, -12.77) * mm, "end": v(-15.5, -12.77) * mm});
            skLineSegment(sketch, "E72.left", {"start": v(-30.5, 6.23) * mm, "end": v(-30.5, -12.77) * mm});
            skLineSegment(sketch, "E72.right", {"start": v(-15.5, 6.23) * mm, "end": v(-15.5, -12.77) * mm});
            skLineSegment(sketch, "E73.bottom", {"start": v(-31.42, 7.37) * mm, "end": v(-14.47, 7.37) * mm});
            skLineSegment(sketch, "E73.top", {"start": v(-31.42, -13.97) * mm, "end": v(-14.47, -13.97) * mm});
            skLineSegment(sketch, "E73.left", {"start": v(-31.42, 7.37) * mm, "end": v(-31.42, -13.97) * mm});
            skLineSegment(sketch, "E73.right", {"start": v(-14.47, 7.37) * mm, "end": v(-14.47, -13.97) * mm});
            skSolve(sketch);
        }
        {
            var Q0;
            Q0=makeQuery(id+"F30.imprint","IMPRINT",FACE,{"disambiguationData":[TD([[makeQuery(id+"F30.imprint","IMPRINT",EDGE,{"derivedFrom":sQuery(id+"F30.wireOp",EDGE,"E72.bottom")}),-1.0]])]});
            extrude(context, id + "F31", {"entities" : qUnion([Q0]), "operationType" : NewBodyOperationType.ADD, "oppositeDirection" : true, "depth" : 1 * mm, "offsetDistance" : 25 * mm});
        }
        {
            var Q0;
            Q0=makeQuery(id+"F18.opExtrude","SWEPT_FACE",FACE,{"disambiguationData":[OSD([sQuery(id+"F17.wireOp",EDGE,"E36")])]});
            extrude(context, id + "F32", {"entities" : qUnion([Q0]), "operationType" : NewBodyOperationType.REMOVE, "depth" : 15 * mm, "offsetDistance" : 25 * mm});
        }
        {
            var Q0;
            Q0=makeQuery(id+"F31.opExtrude","SWEPT_FACE",FACE,{"disambiguationData":[OSD([sQuery(id+"F30.wireOp",EDGE,"E73.left")])]});
            var sketch = newSketch(context, id + "F33", { "sketchPlane" : qUnion([Q0])});
            skLineSegment(sketch, "E74", {"start": v(-13.97, -30.4) * mm, "end": v(-17.3, -30.36) * mm});
            skLineSegment(sketch, "E75", {"start": v(-17.3, -30.36) * mm, "end": v(-17.3, -49.4) * mm});
            skLineSegment(sketch, "E76", {"start": v(-17.3, -49.4) * mm, "end": v(-3.86, -49.4) * mm});
            skLineSegment(sketch, "E77", {"start": v(-3.86, -49.4) * mm, "end": v(7.37, -30.4) * mm});
            skLineSegment(sketch, "E78", {"start": v(7.37, -30.4) * mm, "end": v(-13.97, -30.4) * mm});
            skLineSegment(sketch, "E79", {"start": v(-12.02, -30.4) * mm, "end": v(-17.3, -42.87) * mm});
            skLineSegment(sketch, "E80", {"start": v(6.21, -30.4) * mm, "end": v(-4.44, -48.4) * mm});
            skLineSegment(sketch, "E81", {"start": v(-4.44, -48.4) * mm, "end": v(-17.3, -48.4) * mm});
            skLineSegment(sketch, "E82", {"start": v(-13.97, -29.4) * mm, "end": v(-17.3, -29.4) * mm});
            skLineSegment(sketch, "E83", {"start": v(-17.3, -29.4) * mm, "end": v(-17.3, -30.36) * mm});
            skLineSegment(sketch, "E84", {"start": v(-17.3, -42.87) * mm, "end": v(0, -42.87) * mm});
            skSolve(sketch);
        }
        {
            var Q0;
            {var subQ1=sQuery(id+"F33.wireOp",EDGE,"E79");Q0=makeQuery(id+"F33.imprint","IMPRINT",FACE,{"disambiguationData":[TD([[makeQuery(id+"F33.imprint","IMPRINT",EDGE,{"derivedFrom":subQ1}),1.0]])]});}
            var Q1;
            {var subQ0=sQuery(id+"F33.wireOp",EDGE,"E74");Q1=makeQuery(id+"F33.imprint","IMPRINT",FACE,{"disambiguationData":[TD([[makeQuery(id+"F33.imprint","IMPRINT",EDGE,{"derivedFrom":subQ0}),1.0]])]});}
            var Q2;
            {var subQ0=sQuery(id+"F33.wireOp",EDGE,"E78");var subQ5=sQuery(id+"F33.wireOp",EDGE,"E80");var subQ6=makeQuery(id+"F33.imprint","INTERSECT",VERTEX,{"derivedFrom":[subQ0,subQ5]});Q2=makeQuery(id+"F33.imprint","IMPRINT",FACE,{"disambiguationData":[TD([[makeQuery(id+"F33.imprint","IMPRINT",EDGE,{"disambiguationData":[TD([[subQ6,-1.0]])],"derivedFrom":subQ5}),1.0]])]});}
            extrude(context, id + "F34", {"entities" : qUnion([Q0, Q1, Q2]), "operationType" : NewBodyOperationType.ADD, "oppositeDirection" : true, "depth" : 17 * mm, "offsetDistance" : 25 * mm});
        }
        {
            var Q0;
            {var subQ1=sQuery(id+"F33.wireOp",EDGE,"E79");Q0=makeQuery(id+"F33.imprint","IMPRINT",FACE,{"disambiguationData":[TD([[makeQuery(id+"F33.imprint","IMPRINT",EDGE,{"derivedFrom":subQ1}),1.0]])]});}
            extrude(context, id + "F35", {"entities" : qUnion([Q0]), "operationType" : NewBodyOperationType.REMOVE, "oppositeDirection" : true, "depth" : 16 * mm, "offsetDistance" : 25 * mm, "hasSecondDirection" : true, "secondDirectionOppositeDirection" : true, "secondDirectionDepth" : 1 * mm});
        }
        {
            var Q0;
            {var subQ0=sQuery(id+"F26.wireOp",EDGE,"E63");Q0=makeQuery(id+"F26.imprint","IMPRINT",FACE,{"disambiguationData":[TD([[makeQuery(id+"F26.imprint","IMPRINT",EDGE,{"derivedFrom":subQ0}),1.0]])]});}
            var Q1;
            Q1=sQuery(id+"F26.wireOp",EDGE,"E71");
            revolve(context, id + "F36", {"operationType" : NewBodyOperationType.REMOVE, "surfaceOperationType" : NewSurfaceOperationType.NEW, "entities" : qUnion([Q0]), "axis" : qUnion([Q1]), "revolveType" : RevolveType.ONE_DIRECTION, "oppositeDirection" : true, "angle" : 68 * degree});
        }
        {
            var Q0;
            Q0=makeQuery(id+"F19.imprint","IMPRINT",FACE,{"disambiguationData":[TD([[makeQuery(id+"F19.imprint","IMPRINT",EDGE,{"derivedFrom":sQuery(id+"F19.wireOp",EDGE,"E62.top")}),-1.0]])]});
            extrude(context, id + "F37", {"entities" : qUnion([Q0]), "operationType" : NewBodyOperationType.REMOVE, "oppositeDirection" : true, "depth" : 58.1 * mm, "offsetDistance" : 25 * mm});
        }
        {
            var Q0;
            {var subQ1=sQuery(id+"F19.wireOp",EDGE,"E62.bottom");Q0=makeQuery(id+"F35.boolean.opBoolean","SPLIT",FACE,{"disambiguationData":[TD([makeQuery(id+"F28.boolean.opBoolean","COPY",FACE,{"disambiguationData":[OD(1.0)],"derivedFrom":makeQuery(id+"F28.opRevolve","SWEPT_FACE",FACE,{"disambiguationData":[OSD([sQuery(id+"F26.wireOp",EDGE,"E70")])]})})])],"derivedFrom":makeQuery(id+"F34.boolean.opBoolean","MERGE",FACE,{"derivedFrom":[makeQuery(id+"F21.boolean.opBoolean","MERGE",FACE,{"derivedFrom":[makeQuery(id+"F20.opExtrude","SWEPT_FACE",FACE,{"disambiguationData":[OSD([subQ1])]}),makeQuery(id+"F21.opExtrude","SWEPT_FACE",FACE,{"disambiguationData":[OSD([subQ1])]})]}),makeQuery(id+"F34.opExtrude","SWEPT_FACE",FACE,{"disambiguationData":[OSD([sQuery(id+"F33.wireOp",EDGE,"E75")])]})]})});}
            extrude(context, id + "F38", {"entities" : qUnion([Q0]), "operationType" : NewBodyOperationType.REMOVE, "oppositeDirection" : true, "depth" : 25 * mm, "offsetDistance" : 25 * mm});
        }
    });
